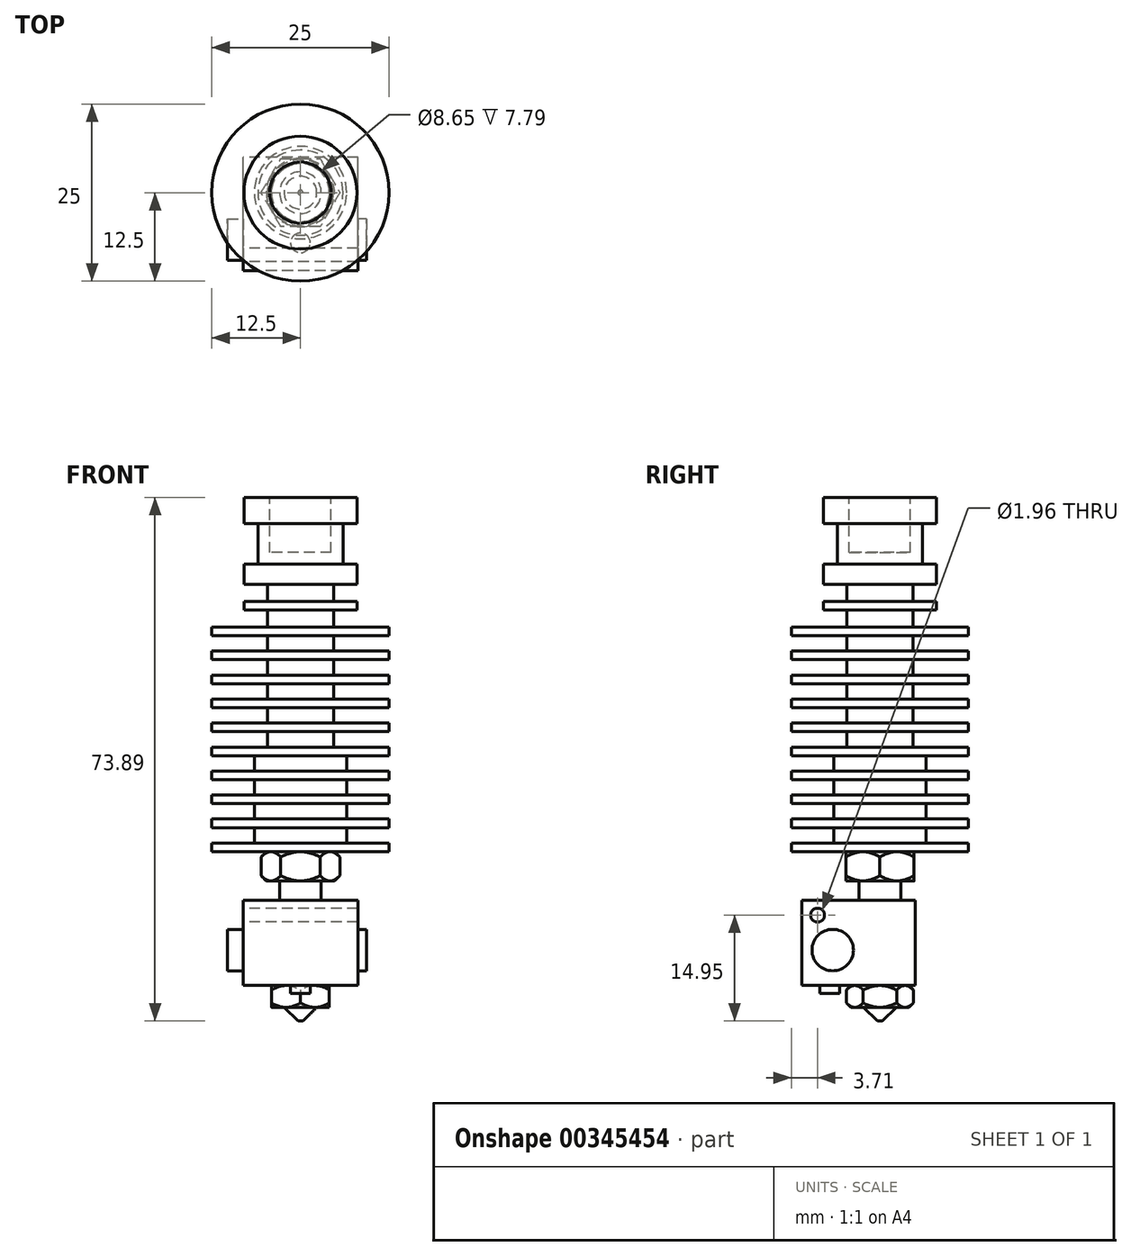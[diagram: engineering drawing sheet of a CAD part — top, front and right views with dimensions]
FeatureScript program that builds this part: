
annotation { "Feature Type Name" : "Feature", "Feature Type Description" : "" }
export const myFeature = defineFeature(function(context is Context, id is Id, definition is map)
    precondition{}
    {
        {
            var Q0;
            Q0=qCreatedBy(makeId("Front.planeOp"),FACE);
            var sketch = newSketch(context, id + "F0", { "sketchPlane" : qUnion([Q0]), "disableImprinting" : false});
            skLineSegment(sketch, "E0", {"start": v(0, 0) * mm, "end": v(0, -73.89) * mm});
            skLineSegment(sketch, "E1", {"start": v(0, -7.79) * mm, "end": v(-4.32, -7.8) * mm});
            skLineSegment(sketch, "E2", {"start": v(-4.33, 0) * mm, "end": v(-4.33, -7.8) * mm});
            skLineSegment(sketch, "E3", {"start": v(-4.33, 0) * mm, "end": v(-7.97, 0) * mm});
            skLineSegment(sketch, "E4", {"start": v(-7.97, 0) * mm, "end": v(-7.97, -3.67) * mm});
            skLineSegment(sketch, "E5", {"start": v(-7.97, -3.67) * mm, "end": v(-6, -3.67) * mm});
            skLineSegment(sketch, "E6", {"start": v(-6, -3.67) * mm, "end": v(-6, -9.4) * mm});
            skLineSegment(sketch, "E7", {"start": v(-6, -9.4) * mm, "end": v(-7.97, -9.4) * mm});
            skLineSegment(sketch, "E8", {"start": v(-7.97, -9.4) * mm, "end": v(-7.97, -12.3) * mm});
            skLineSegment(sketch, "E9", {"start": v(-7.97, -12.3) * mm, "end": v(-4.66, -12.3) * mm});
            skLineSegment(sketch, "E10", {"start": v(-4.66, -12.3) * mm, "end": v(-4.66, -14.7) * mm});
            skLineSegment(sketch, "E11", {"start": v(-4.66, -15.9) * mm, "end": v(-4.66, -18.3) * mm});
            skLineSegment(sketch, "E12", {"start": v(-4.66, -18.3) * mm, "end": v(-12.5, -18.3) * mm});
            skLineSegment(sketch, "E13", {"start": v(-12.5, -50) * mm, "end": v(-2.94, -50) * mm});
            skLineSegment(sketch, "E14", {"start": v(-2.94, -50) * mm, "end": v(-2.94, -71.96) * mm});
            skLineSegment(sketch, "E15", {"start": v(-2.3, -71.96) * mm, "end": v(-2.94, -71.96) * mm});
            skLineSegment(sketch, "E16", {"start": v(-2.3, -71.96) * mm, "end": v(-0.35, -73.89) * mm});
            skLineSegment(sketch, "E17", {"start": v(-0.35, -73.89) * mm, "end": v(0, -73.89) * mm});
            skLineSegment(sketch, "E18", {"start": v(0, 0) * mm, "end": v(0, -7.79) * mm});
            skLineSegment(sketch, "E19", {"start": v(-4.66, -14.7) * mm, "end": v(-7.97, -14.7) * mm});
            skLineSegment(sketch, "E20", {"start": v(-7.97, -14.7) * mm, "end": v(-7.97, -15.9) * mm});
            skLineSegment(sketch, "E21", {"start": v(-7.97, -15.9) * mm, "end": v(-4.66, -15.9) * mm});
            skCircle(sketch, "E22", {"center": v(-12.5, -20) * mm, "radius": 1.7 * mm, "construction": true});
            skLineSegment(sketch, "E23", {"start": v(-12.5, -18.3) * mm, "end": v(-14.2, -18.3) * mm, "construction": true});
            skLineSegment(sketch, "E24", {"start": v(-14.2, -18.3) * mm, "end": v(-14.2, -50) * mm, "construction": true});
            skLineSegment(sketch, "E25", {"start": v(-14.2, -50) * mm, "end": v(-12.5, -50) * mm, "construction": true});
            skCircle(sketch, "E26", {"center": v(-12.5, -23.38) * mm, "radius": 1.7 * mm, "construction": true});
            skCircle(sketch, "E27", {"center": v(-12.5, -26.76) * mm, "radius": 1.7 * mm, "construction": true});
            skCircle(sketch, "E28", {"center": v(-12.5, -30.15) * mm, "radius": 1.7 * mm, "construction": true});
            skCircle(sketch, "E29", {"center": v(-12.5, -33.53) * mm, "radius": 1.7 * mm, "construction": true});
            skCircle(sketch, "E30", {"center": v(-12.5, -36.92) * mm, "radius": 1.7 * mm, "construction": true});
            skCircle(sketch, "E31", {"center": v(-12.5, -40.3) * mm, "radius": 1.7 * mm, "construction": true});
            skCircle(sketch, "E32", {"center": v(-12.5, -43.7) * mm, "radius": 1.7 * mm, "construction": true});
            skLineSegment(sketch, "E33", {"start": v(-12.5, -18.3) * mm, "end": v(-12.5, -50) * mm, "construction": true});
            skCircle(sketch, "E34", {"center": v(-7.97, -15.3) * mm, "radius": 3 * mm, "construction": true});
            skLineSegment(sketch, "E35", {"start": v(-12.5, -18.3) * mm, "end": v(-12.5, -19.52) * mm});
            skLineSegment(sketch, "E36", {"start": v(-12.5, -19.52) * mm, "end": v(-4.66, -19.52) * mm});
            skLineSegment(sketch, "E37", {"start": v(-4.66, -19.52) * mm, "end": v(-4.66, -21.69) * mm});
            skLineSegment(sketch, "E38", {"start": v(-4.66, -21.69) * mm, "end": v(-12.5, -21.69) * mm});
            skLineSegment(sketch, "E39", {"start": v(-13.11, -18.3) * mm, "end": v(-13.1, -50) * mm, "construction": true});
            skCircle(sketch, "E40", {"center": v(-12.5, -47.08) * mm, "radius": 1.7 * mm, "construction": true});
            skLineSegment(sketch, "E41", {"start": v(-12.5, -50) * mm, "end": v(-12.5, -48.77) * mm});
            skLineSegment(sketch, "E42", {"start": v(-12.5, -48.77) * mm, "end": v(-6.52, -48.77) * mm});
            skLineSegment(sketch, "E43", {"start": v(-6.52, -48.77) * mm, "end": v(-6.52, -46.6) * mm});
            skCircle(sketch, "E44", {"center": v(-12.5, -49.38) * mm, "radius": 0.61 * mm, "construction": true});
            skCircle(sketch, "E45", {"center": v(-12.5, -18.9) * mm, "radius": 0.61 * mm, "construction": true});
            skCircle(sketch, "E46", {"center": v(-12.5, -22.3) * mm, "radius": 0.61 * mm, "construction": true});
            skCircle(sketch, "E47", {"center": v(-12.5, -25.68) * mm, "radius": 0.61 * mm, "construction": true});
            skCircle(sketch, "E48", {"center": v(-12.5, -29.07) * mm, "radius": 0.61 * mm, "construction": true});
            skCircle(sketch, "E49", {"center": v(-12.5, -32.45) * mm, "radius": 0.61 * mm, "construction": true});
            skCircle(sketch, "E50", {"center": v(-12.5, -35.84) * mm, "radius": 0.61 * mm, "construction": true});
            skCircle(sketch, "E51", {"center": v(-12.5, -39.22) * mm, "radius": 0.61 * mm, "construction": true});
            skCircle(sketch, "E52", {"center": v(-12.5, -42.6) * mm, "radius": 0.61 * mm, "construction": true});
            skCircle(sketch, "E53", {"center": v(-12.5, -46) * mm, "radius": 0.61 * mm, "construction": true});
            skLineSegment(sketch, "E54", {"start": v(-6.52, -46.6) * mm, "end": v(-12.5, -46.6) * mm});
            skLineSegment(sketch, "E55", {"start": v(-12.5, -46.6) * mm, "end": v(-12.5, -45.38) * mm});
            skLineSegment(sketch, "E56", {"start": v(-12.5, -45.38) * mm, "end": v(-6.52, -45.38) * mm});
            skLineSegment(sketch, "E57", {"start": v(-6.52, -45.38) * mm, "end": v(-6.52, -43.22) * mm});
            skLineSegment(sketch, "E58", {"start": v(-6.52, -43.22) * mm, "end": v(-12.5, -43.22) * mm});
            skLineSegment(sketch, "E59", {"start": v(-12.5, -43.22) * mm, "end": v(-12.5, -42) * mm});
            skLineSegment(sketch, "E60", {"start": v(-12.5, -42) * mm, "end": v(-6.52, -42) * mm});
            skLineSegment(sketch, "E61", {"start": v(-12.5, -38.61) * mm, "end": v(-12.5, -39.83) * mm});
            skLineSegment(sketch, "E62", {"start": v(-12.5, -39.83) * mm, "end": v(-6.52, -39.83) * mm});
            skLineSegment(sketch, "E63", {"start": v(-6.52, -39.83) * mm, "end": v(-6.52, -42) * mm});
            skLineSegment(sketch, "E64", {"start": v(-12.5, -38.61) * mm, "end": v(-6.52, -38.61) * mm});
            skLineSegment(sketch, "E65", {"start": v(-6.52, -38.61) * mm, "end": v(-6.52, -36.45) * mm});
            skLineSegment(sketch, "E66", {"start": v(-6.52, -36.45) * mm, "end": v(-12.5, -36.45) * mm});
            skLineSegment(sketch, "E67", {"start": v(-12.5, -36.45) * mm, "end": v(-12.5, -35.23) * mm});
            skLineSegment(sketch, "E68", {"start": v(-12.5, -35.23) * mm, "end": v(-4.66, -35.23) * mm});
            skLineSegment(sketch, "E69", {"start": v(-4.66, -35.23) * mm, "end": v(-4.66, -33.06) * mm});
            skLineSegment(sketch, "E70", {"start": v(-4.66, -33.06) * mm, "end": v(-12.5, -33.06) * mm});
            skLineSegment(sketch, "E71", {"start": v(-12.5, -33.06) * mm, "end": v(-12.5, -31.84) * mm});
            skLineSegment(sketch, "E72", {"start": v(-12.5, -21.69) * mm, "end": v(-12.5, -22.9) * mm});
            skLineSegment(sketch, "E73", {"start": v(-12.5, -22.9) * mm, "end": v(-4.66, -22.9) * mm});
            skLineSegment(sketch, "E74", {"start": v(-4.66, -22.9) * mm, "end": v(-4.66, -25.07) * mm});
            skLineSegment(sketch, "E75", {"start": v(-4.66, -25.07) * mm, "end": v(-12.5, -25.07) * mm});
            skLineSegment(sketch, "E76", {"start": v(-12.5, -25.07) * mm, "end": v(-12.5, -26.3) * mm});
            skLineSegment(sketch, "E77", {"start": v(-12.5, -26.3) * mm, "end": v(-4.66, -26.3) * mm});
            skLineSegment(sketch, "E78", {"start": v(-4.66, -26.3) * mm, "end": v(-4.66, -28.46) * mm});
            skLineSegment(sketch, "E79", {"start": v(-4.66, -28.46) * mm, "end": v(-12.5, -28.46) * mm});
            skLineSegment(sketch, "E80", {"start": v(-12.5, -28.46) * mm, "end": v(-12.5, -29.68) * mm});
            skLineSegment(sketch, "E81", {"start": v(-12.5, -31.84) * mm, "end": v(-4.66, -31.84) * mm});
            skLineSegment(sketch, "E82", {"start": v(-4.66, -31.84) * mm, "end": v(-4.66, -29.68) * mm});
            skLineSegment(sketch, "E83", {"start": v(-4.66, -29.68) * mm, "end": v(-12.5, -29.68) * mm});
            skSolve(sketch);
        }
        {
            var Q0;
            Q0=makeQuery(id+"F0.imprint","IMPRINT",FACE,{"disambiguationData":[TD([[makeQuery(id+"F0.imprint","IMPRINT",EDGE,{"derivedFrom":sQuery(id+"F0.wireOp",EDGE,"E0")}),-1.0]])]});
            var Q1;
            Q1=sQuery(id+"F0.wireOp",EDGE,"E0");
            revolve(context, id + "F1", {"entities" : qUnion([Q0]), "axis" : qUnion([Q1]), "revolveType" : RevolveType.FULL});
        }
        {
            var Q0;
            Q0=makeQuery(id+"F1.opRevolve","SWEPT_FACE",FACE,{"disambiguationData":[OSD([sQuery(id+"F0.wireOp",EDGE,"E15")])]});
            var sketch = newSketch(context, id + "F2", { "sketchPlane" : qUnion([Q0])});
            skCircle(sketch, "E84.cCircle", {"center": v(0, 0) * mm, "radius": 4.08 * mm, "construction": true});
            skLineSegment(sketch, "E84.0", {"start": v(-4.08, -2.36) * mm, "end": v(-4.08, 2.36) * mm});
            skLineSegment(sketch, "E84.1", {"start": v(-4.08, 2.36) * mm, "end": v(0, 4.72) * mm});
            skLineSegment(sketch, "E84.2", {"start": v(0, 4.72) * mm, "end": v(4.08, 2.36) * mm});
            skLineSegment(sketch, "E84.3", {"start": v(4.08, 2.36) * mm, "end": v(4.09, -2.36) * mm});
            skLineSegment(sketch, "E84.4", {"start": v(4.09, -2.36) * mm, "end": v(0, -4.72) * mm});
            skLineSegment(sketch, "E84.5", {"start": v(0, -4.72) * mm, "end": v(-4.08, -2.36) * mm});
            skPoint(sketch, "E84.0.midPoint", {"position": v(-4.08, 0) * mm});
            skSolve(sketch);
        }
        {
            var Q0;
            Q0 = qSketchRegion(id + "F2", true);
            extrude(context, id + "F3", {"entities" : qUnion([Q0]), "operationType" : NewBodyOperationType.ADD, "oppositeDirection" : true, "depth" : 3.09 * mm});
        }
        {
            var Q0;
            Q0=qCreatedBy(makeId("Front.planeOp"),FACE);
            var sketch = newSketch(context, id + "F4", { "sketchPlane" : qUnion([Q0])});
            skLineSegment(sketch, "E85.0", {"start": v(-4.08, -68.87) * mm, "end": v(-4.08, -71.96) * mm, "construction": true});
            skLineSegment(sketch, "E86", {"start": v(-4.08, -71.96) * mm, "end": v(-5.63, -70.42) * mm});
            skLineSegment(sketch, "E87", {"start": v(-5.63, -70.42) * mm, "end": v(-4.09, -68.87) * mm});
            skLineSegment(sketch, "E88", {"start": v(-5.63, -70.42) * mm, "end": v(-4.08, -70.42) * mm, "construction": true});
            skLineSegment(sketch, "E89", {"start": v(0, -68.87) * mm, "end": v(0, -76.05) * mm, "construction": true});
            skLineSegment(sketch, "E90", {"start": v(0, -76.05) * mm, "end": v(-4.08, -71.96) * mm, "construction": true});
            skLineSegment(sketch, "E91", {"start": v(-4.08, -71.96) * mm, "end": v(-4.08, -72.96) * mm});
            skLineSegment(sketch, "E92", {"start": v(-4.08, -72.96) * mm, "end": v(-7.09, -72.96) * mm});
            skLineSegment(sketch, "E93", {"start": v(-7.08, -72.96) * mm, "end": v(-7.08, -67.87) * mm});
            skLineSegment(sketch, "E94", {"start": v(-7.09, -67.87) * mm, "end": v(-4.08, -67.87) * mm});
            skLineSegment(sketch, "E95", {"start": v(-4.08, -67.87) * mm, "end": v(-4.08, -68.87) * mm});
            skSolve(sketch);
        }
        {
            var Q0;
            Q0 = qSketchRegion(id + "F4", true);
            var Q1;
            Q1=sQuery(id+"F4.wireOp",EDGE,"E89");
            revolve(context, id + "F5", {"operationType" : NewBodyOperationType.REMOVE, "entities" : qUnion([Q0]), "axis" : qUnion([Q1]), "revolveType" : RevolveType.FULL, "oppositeDirection" : true});
        }
        {
            var Q0;
            Q0=makeQuery(id+"F3.opExtrude","CAP_FACE",FACE,{"disambiguationData":[OSD([sQuery(id+"F2.wireOp",EDGE,"E84.0"),sQuery(id+"F2.wireOp",EDGE,"E84.1"),sQuery(id+"F2.wireOp",EDGE,"E84.2"),sQuery(id+"F2.wireOp",EDGE,"E84.3"),sQuery(id+"F2.wireOp",EDGE,"E84.4"),sQuery(id+"F2.wireOp",EDGE,"E84.5")])],"isStart":false});
            var sketch = newSketch(context, id + "F6", { "sketchPlane" : qUnion([Q0])});
            skLineSegment(sketch, "E96", {"start": v(0, -11.04) * mm, "end": v(-8.1, -11.04) * mm});
            skLineSegment(sketch, "E97", {"start": v(-8.1, -11.04) * mm, "end": v(-8.1, 4.98) * mm});
            skLineSegment(sketch, "E98", {"start": v(-8.1, 4.98) * mm, "end": v(0, 4.98) * mm});
            skLineSegment(sketch, "E99", {"start": v(0, 4.98) * mm, "end": v(0, 0) * mm, "construction": true});
            skLineSegment(sketch, "E100", {"start": v(0, 0) * mm, "end": v(0, -11.04) * mm, "construction": true});
            skLineSegment(sketch, "E101", {"start": v(0, 4.98) * mm, "end": v(0, 12.5) * mm, "construction": true});
            skCircle(sketch, "E102.0", {"center": v(0, 0) * mm, "radius": 12.5 * mm, "construction": true});
            skLineSegment(sketch, "E103.MirrorCS", {"start": v(0, -11.04) * mm, "end": v(8.1, -11.04) * mm});
            skLineSegment(sketch, "E104.MirrorCS", {"start": v(8.1, -11.04) * mm, "end": v(8.1, 4.98) * mm});
            skLineSegment(sketch, "E105.MirrorCS", {"start": v(8.1, 4.98) * mm, "end": v(0, 4.98) * mm});
            skSolve(sketch);
        }
        {
            var Q0;
            Q0 = qSketchRegion(id + "F6", true);
            extrude(context, id + "F7", {"entities" : qUnion([Q0]), "operationType" : NewBodyOperationType.ADD, "depth" : 12.02 * mm});
        }
        {
            var Q0;
            Q0=makeQuery(id+"F7.opExtrude","SWEPT_FACE",FACE,{"disambiguationData":[OSD([sQuery(id+"F6.wireOp",EDGE,"E97")])]});
            var sketch = newSketch(context, id + "F8", { "sketchPlane" : qUnion([Q0])});
            skCircle(sketch, "E106", {"center": v(6.65, -63.88) * mm, "radius": 2.92 * mm});
            skCircle(sketch, "E107", {"center": v(8.79, -58.94) * mm, "radius": 0.98 * mm});
            skSolve(sketch);
        }
        {
            var Q0;
            Q0=makeQuery(id+"F8.imprint","IMPRINT",FACE,{"disambiguationData":[TD([[makeQuery(id+"F8.imprint","IMPRINT",EDGE,{"derivedFrom":sQuery(id+"F8.wireOp",EDGE,"E107")}),1.0]])]});
            extrude(context, id + "F9", {"entities" : qUnion([Q0]), "operationType" : NewBodyOperationType.REMOVE, "endBound" : BoundingType.THROUGH_ALL, "oppositeDirection" : true, "depth" : 25 * mm});
        }
        {
            var Q0;
            Q0=makeQuery(id+"F8.imprint","IMPRINT",FACE,{"disambiguationData":[TD([[makeQuery(id+"F8.imprint","IMPRINT",EDGE,{"derivedFrom":sQuery(id+"F8.wireOp",EDGE,"E106")}),1.0]])]});
            extrude(context, id + "F10", {"entities" : qUnion([Q0]), "operationType" : NewBodyOperationType.ADD, "depth" : 2.17 * mm});
        }
        {
            var Q0;
            Q0=makeQuery(id+"F10.opExtrude","CAP_FACE",FACE,{"disambiguationData":[OSD([sQuery(id+"F8.wireOp",EDGE,"E106")])],"isStart":false});
            extrude(context, id + "F11", {"entities" : qUnion([Q0]), "operationType" : NewBodyOperationType.ADD, "oppositeDirection" : true, "depth" : 19.62 * mm});
        }
        {
            var Q0;
            Q0=makeQuery(id+"F7.opExtrude","CAP_FACE",FACE,{"disambiguationData":[OSD([sQuery(id+"F6.wireOp",EDGE,"E96"),sQuery(id+"F6.wireOp",EDGE,"E97"),sQuery(id+"F6.wireOp",EDGE,"E98"),sQuery(id+"F6.wireOp",EDGE,"E103.MirrorCS"),sQuery(id+"F6.wireOp",EDGE,"E104.MirrorCS"),sQuery(id+"F6.wireOp",EDGE,"E105.MirrorCS")])],"isStart":true});
            var sketch = newSketch(context, id + "F12", { "sketchPlane" : qUnion([Q0])});
            skLineSegment(sketch, "E108", {"start": v(0, 0) * mm, "end": v(0, 11.04) * mm, "construction": true});
            skCircle(sketch, "E109", {"center": v(0, 7.08) * mm, "radius": 1.39 * mm});
            skSolve(sketch);
        }
        {
            var Q0;
            Q0 = qSketchRegion(id + "F12", true);
            extrude(context, id + "F13", {"entities" : qUnion([Q0]), "operationType" : NewBodyOperationType.ADD, "depth" : 1.12 * mm});
        }
        {
            var Q0;
            Q0=makeQuery(id+"F1.opRevolve","SWEPT_FACE",FACE,{"disambiguationData":[OSD([sQuery(id+"F0.wireOp",EDGE,"E13")])]});
            var sketch = newSketch(context, id + "F14", { "sketchPlane" : qUnion([Q0])});
            skCircle(sketch, "E110.cCircle", {"center": v(0, 0) * mm, "radius": 4.8 * mm, "construction": true});
            skLineSegment(sketch, "E110.0", {"start": v(-2.78, 4.8) * mm, "end": v(2.78, 4.8) * mm});
            skLineSegment(sketch, "E110.1", {"start": v(2.78, 4.81) * mm, "end": v(5.55, 0) * mm});
            skLineSegment(sketch, "E110.2", {"start": v(5.55, 0) * mm, "end": v(2.78, -4.8) * mm});
            skLineSegment(sketch, "E110.3", {"start": v(2.78, -4.8) * mm, "end": v(-2.78, -4.81) * mm});
            skLineSegment(sketch, "E110.4", {"start": v(-2.78, -4.81) * mm, "end": v(-5.55, 0) * mm});
            skLineSegment(sketch, "E110.5", {"start": v(-5.55, 0) * mm, "end": v(-2.78, 4.8) * mm});
            skPoint(sketch, "E110.0.midPoint", {"position": v(0, 4.8) * mm});
            skSolve(sketch);
        }
        {
            var Q0;
            Q0 = qSketchRegion(id + "F14", true);
            extrude(context, id + "F15", {"entities" : qUnion([Q0]), "operationType" : NewBodyOperationType.ADD, "depth" : 4.13 * mm});
        }
        {
            var Q0;
            Q0=qCreatedBy(makeId("Right.planeOp"),FACE);
            var sketch = newSketch(context, id + "F16", { "sketchPlane" : qUnion([Q0])});
            skLineSegment(sketch, "E111", {"start": v(0, 0) * mm, "end": v(0, -58.93) * mm, "construction": true});
            skLineSegment(sketch, "E112", {"start": v(0, -58.93) * mm, "end": v(6.88, -52.06) * mm});
            skLineSegment(sketch, "E113", {"start": v(6.88, -52.06) * mm, "end": v(4.81, -50) * mm});
            skLineSegment(sketch, "E114.0", {"start": v(4.81, -54.12) * mm, "end": v(4.81, -50) * mm, "construction": true});
            skLineSegment(sketch, "E115", {"start": v(4.81, -52.06) * mm, "end": v(6.88, -52.06) * mm, "construction": true});
            skLineSegment(sketch, "E116", {"start": v(4.81, -50) * mm, "end": v(8.81, -50) * mm});
            skLineSegment(sketch, "E117", {"start": v(8.81, -50) * mm, "end": v(8.81, -54.12) * mm});
            skLineSegment(sketch, "E118", {"start": v(8.81, -54.12) * mm, "end": v(4.81, -54.12) * mm});
            skSolve(sketch);
        }
        {
            var Q0;
            Q0 = qSketchRegion(id + "F16", true);
            var Q1;
            Q1=sQuery(id+"F16.wireOp",EDGE,"E111");
            revolve(context, id + "F17", {"operationType" : NewBodyOperationType.REMOVE, "entities" : qUnion([Q0]), "axis" : qUnion([Q1]), "revolveType" : RevolveType.FULL, "oppositeDirection" : true});
        }
    });
